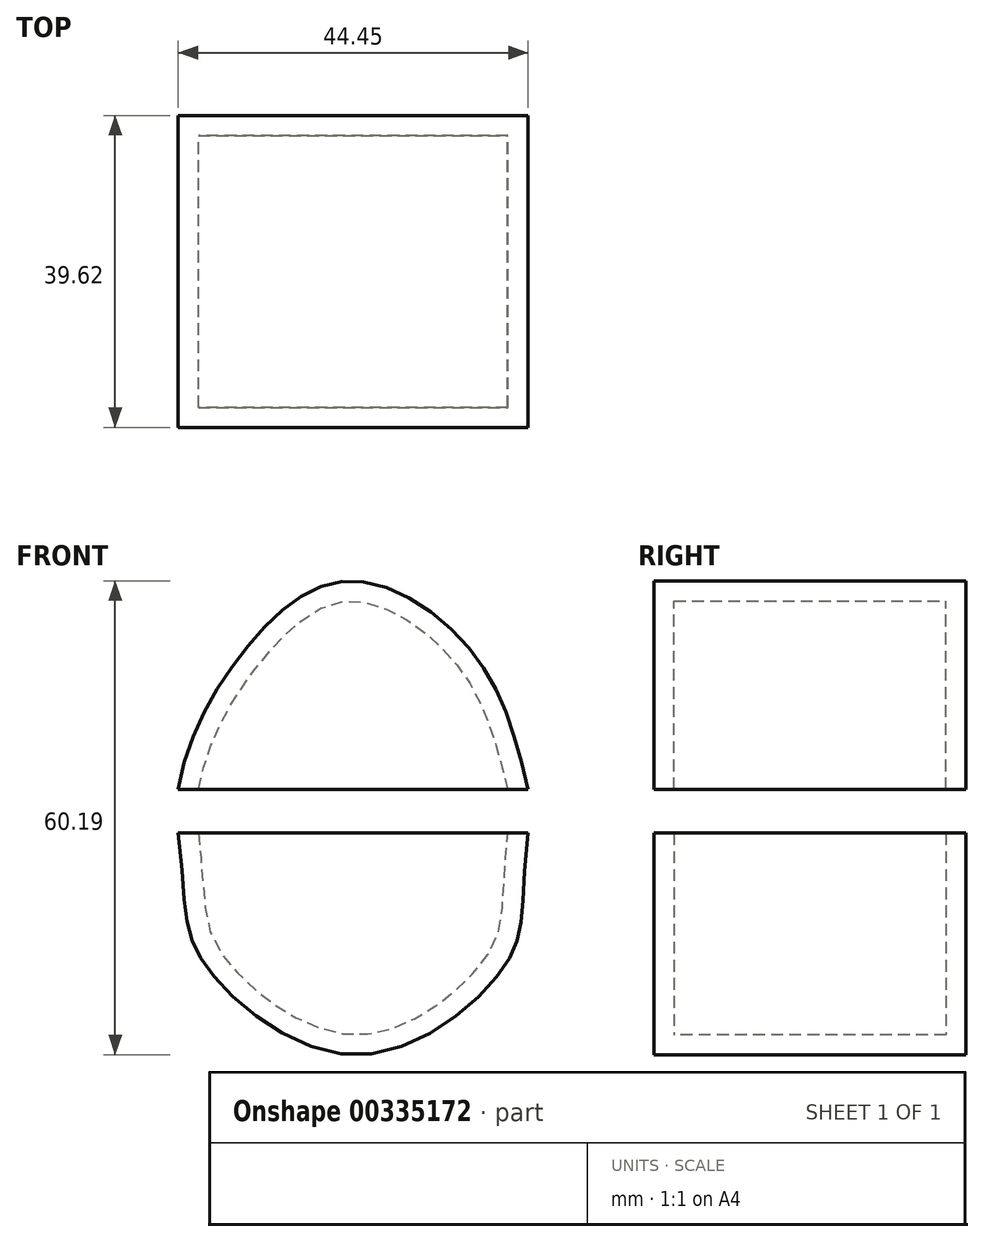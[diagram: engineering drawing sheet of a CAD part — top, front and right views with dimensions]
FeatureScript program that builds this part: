
annotation { "Feature Type Name" : "Feature", "Feature Type Description" : "" }
export const myFeature = defineFeature(function(context is Context, id is Id, definition is map)
    precondition{}
    {
        {
            var Q0;
            Q0=qCreatedBy(makeId("Front.planeOp"),FACE);
            var sketch = newSketch(context, id + "F0", { "sketchPlane" : qUnion([Q0])});
            skPoint(sketch, "E0", {"position": v(-54.5, 16.7) * mm});
            skPoint(sketch, "E1", {"position": v(-10.04, 16.7) * mm});
            skFitSpline(sketch, "E2", {"points": [v(-54.5, 16.7) * mm, v(-51.12, 0) * mm, v(-31.65, -11.45) * mm, v(-12.92, 0) * mm, v(-10.04, 16.7) * mm], "startDerivative": vector(14.08, -124.69) * mm, "endDerivative": vector(13.9, 127.6) * mm});
            skPoint(sketch, "E3", {"position": v(-54.5, 22.26) * mm});
            skPoint(sketch, "E4", {"position": v(-10.04, 22.26) * mm});
            skFitSpline(sketch, "E5", {"points": [v(-54.5, 22.26) * mm, v(-45.29, 40.87) * mm, v(-32.62, 48.74) * mm, v(-17.46, 40.1) * mm, v(-10.04, 22.26) * mm], "startDerivative": vector(12.84, 79.44) * mm, "endDerivative": vector(19.3, -82.34) * mm});
            skLineSegment(sketch, "E6", {"start": v(-54.5, 22.26) * mm, "end": v(-10.04, 22.26) * mm});
            skLineSegment(sketch, "E7", {"start": v(-10.04, 16.7) * mm, "end": v(-54.5, 16.7) * mm});
            skSolve(sketch);
        }
        {
            var Q0;
            Q0=makeQuery(id+"F0.imprint","IMPRINT",FACE,{"disambiguationData":[TD([[makeQuery(id+"F0.imprint","IMPRINT",EDGE,{"derivedFrom":sQuery(id+"F0.wireOp",EDGE,"E5")}),-1.0]])]});
            var Q1;
            Q1=makeQuery(id+"F0.imprint","IMPRINT",FACE,{"disambiguationData":[TD([[makeQuery(id+"F0.imprint","IMPRINT",EDGE,{"derivedFrom":sQuery(id+"F0.wireOp",EDGE,"E2")}),1.0]])]});
            extrude(context, id + "F1", {"entities" : qUnion([Q0, Q1]), "depth" : 39.62 * mm});
        }
        {
            var Q0;
            Q0=makeQuery(id+"F1.opExtrude","SWEPT_FACE",FACE,{"disambiguationData":[OSD([sQuery(id+"F0.wireOp",EDGE,"E6")])]});
            var Q1;
            Q1=makeQuery(id+"F1.opExtrude","SWEPT_FACE",FACE,{"disambiguationData":[OSD([sQuery(id+"F0.wireOp",EDGE,"E7")])]});
            shell(context, id + "F2", {"entities" : qUnion([Q0, Q1]), "thickness" : 2.54 * mm});
        }
    });
